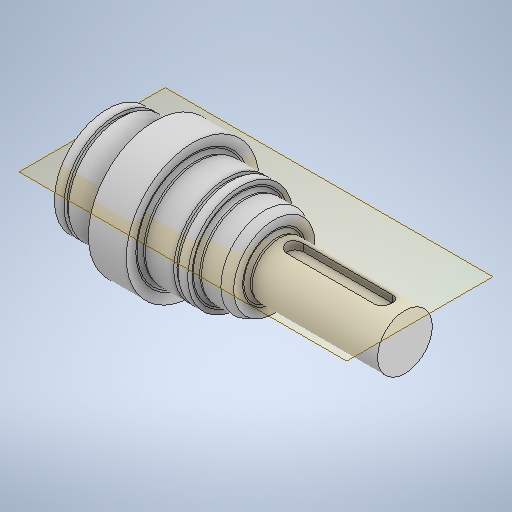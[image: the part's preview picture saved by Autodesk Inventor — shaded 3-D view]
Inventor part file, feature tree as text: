
AUTODESK INVENTOR PART (.ipt)
format: ipt  version: 2025.3 (Build 293356030, 356C)  size: 392,704 bytes
history: native  units: mm
features: sketch x9, revolve x8, chamfer x1, plane x1, extrude x1
ambient origin geometry x8: Origin, YZ Plane, XZ Plane, XY Plane, X Axis, Y Axis, Z Axis, Center Point
bodies: Body1 (feature_tree)
feature tree (20):
  revolve  "Umdrehung20"
  revolve  "Umdrehung21"
  revolve  "Umdrehung22"
  revolve  "Umdrehung23"
  revolve  "Umdrehung24"
  revolve  "Umdrehung25"
  chamfer  "Fasen2"  Distance=1.75mm
  revolve  "Umdrehung26"
  plane  "Arbeitsebene4"
  extrude  "Extrusion4"  Depth=13.0mm
  revolve  "Umdrehung27"
  sketch  "Skizze23"  dims[d31=0.0mm]
  sketch  "Skizze24"  dims[d32=0.0mm]
  sketch  "Skizze25"  dims[d33=0.0mm]
  sketch  "Skizze26"  dims[d34=0.0mm]
  sketch  "Skizze27"  dims[d35=0.0mm]
  sketch  "Skizze28"  dims[d36=0.0mm d37=1.75mm d38=0.125mm d39=19.547688mm]
  sketch  "Skizze29"  dims[d40=0.0mm d41=13.0mm]
  sketch  "Skizze30"  dims[d42=4.0mm d43=0.0mm]
  sketch  "Skizze31"  dims[d44=0.0mm]
